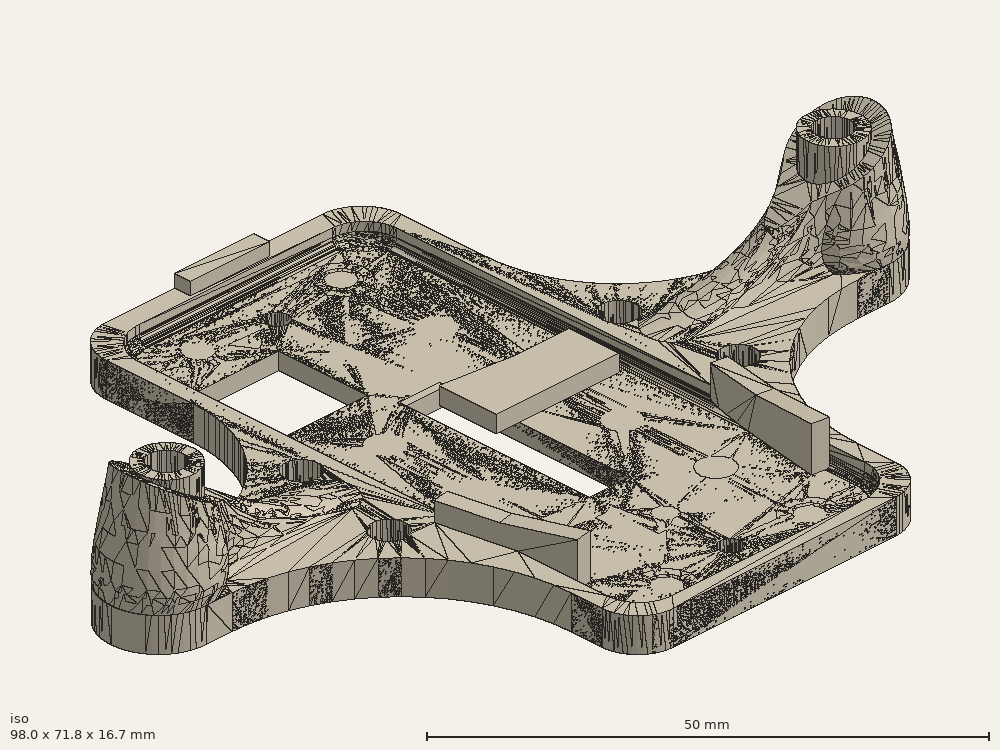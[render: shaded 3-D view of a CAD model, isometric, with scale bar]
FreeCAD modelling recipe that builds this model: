
FCSTD DOCUMENT  (FreeCAD 0.16R5446 (Git))
Label: iris_tarot_ng
License: CC-BY 3.0
LicenseURL: http://creativecommons.org/licenses/by/3.0/
objects: Part::Cylinder×19, Sketcher::SketchObject×15, Part::Cut×10, PartDesign::Pad×6, Part::Feature×4, Part::MultiFuse×4, Part::Loft×2, Part::Box×2, PartDesign::Fillet×2, PartDesign::Pocket×2, Mesh::Feature×1, PartDesign::LinearPattern×1, PartDesign::Chamfer×1
note: 76 computed .brp shape members not serialized (recipe doc carries the construction recipe); baked Part::Feature solids carry a one-line shape summary decoded from their .brp

FEATURE [Mesh::Feature] tarot_with_extra_spacing
FEATURE [Sketcher::SketchObject] Sketch
  Placement = pos=(4.5,0,4) rot=(0,0,1;0rad)
  sketch-geometry (4):
    g0: ArcOfCircle CenterX=-47.4503 CenterY=0 CenterZ=0 NormalX=0 NormalY=0 NormalZ=1 Radius=6 StartAngle=0.685014 EndAngle=5.53331
    g1: ArcOfCircle CenterX=-26.1247 CenterY=0 CenterZ=0 NormalX=0 NormalY=0 NormalZ=1 Radius=3 StartAngle=4.71239 EndAngle=7.61132
    g2: LineSegment StartX=-43.0597 StartY=-4.0893 StartZ=0 EndX=-26.1247 EndY=-3 EndZ=0
    g3: LineSegment StartX=-42.8038 StartY=3.7961 StartZ=0 EndX=-25.4039 EndY=2.91211 EndZ=0
  constraints (8):
    c: PointOnObject(g0,g-1)
    c: Radius(g0) = 6
    c: PointOnObject(g1,g-1)
    c: Radius(g1) = 3
    c: Coincident(g0,g3)
    c: Coincident(g1,g3)
    c: Coincident(g1,g2)
    c: Coincident(g0,g2)
FEATURE [Sketcher::SketchObject] Sketch001
  Placement = pos=(0,0,17) rot=(0,0,1;0rad)
  sketch-geometry (4):
    g0: ArcOfCircle CenterX=-42 CenterY=0 CenterZ=0 NormalX=0 NormalY=0 NormalZ=1 Radius=5 StartAngle=1.5708 EndAngle=4.71239
    g1: ArcOfCircle CenterX=-42 CenterY=0 CenterZ=0 NormalX=0 NormalY=0 NormalZ=1 Radius=4.93488 StartAngle=5.76091 EndAngle=6.78639
    g2: LineSegment StartX=-42 StartY=5 StartZ=0 EndX=-37.6768 EndY=2.37977 EndZ=0
    g3: LineSegment StartX=-42 StartY=-5 StartZ=0 EndX=-37.723 EndY=-2.46177 EndZ=0
  constraints (5):
    c: Radius(g0) = 5
    c: Coincident(g0,g2)
    c: Coincident(g1,g2)
    c: Coincident(g1,g3)
    c: Coincident(g0,g3)
FEATURE [Sketcher::SketchObject] Sketch002
  Placement = pos=(2.5,0,7.5) rot=(0,0,1;0rad)
  sketch-geometry (4):
    g0: ArcOfCircle CenterX=-45.3118 CenterY=0 CenterZ=0 NormalX=0 NormalY=0 NormalZ=1 Radius=6 StartAngle=0.523596 EndAngle=5.75959
    g1: ArcOfCircle CenterX=-35.9224 CenterY=0 CenterZ=0 NormalX=0 NormalY=0 NormalZ=1 Radius=2 StartAngle=4.93357 EndAngle=7.89275
    g2: LineSegment StartX=-40.1156 StartY=-2.99999 StartZ=0 EndX=-35.4836 EndY=-1.95128 EndZ=0
    g3: LineSegment StartX=-40.1156 StartY=2.99999 StartZ=0 EndX=-35.9999 EndY=1.9985 EndZ=0
  constraints (8):
    c: PointOnObject(g0,g-1)
    c: Radius(g0) = 6
    c: PointOnObject(g1,g-1)
    c: Radius(g1) = 2
    c: Coincident(g0,g3)
    c: Coincident(g1,g3)
    c: Coincident(g1,g2)
    c: Coincident(g0,g2)
FEATURE [Sketcher::SketchObject] Sketch003
  Placement = pos=(0,6,0) rot=(1,0,0;1.5708rad)
  sketch-geometry (4):
    g0: LineSegment StartX=-49.773 StartY=18.3055 StartZ=0 EndX=-31.5833 EndY=7.72916 EndZ=0
    g1: LineSegment StartX=-31.5833 StartY=7.72916 StartZ=0 EndX=-31.5833 EndY=19.3543 EndZ=0
    g2: LineSegment StartX=-31.5833 StartY=19.3543 StartZ=0 EndX=-49.773 EndY=19.3543 EndZ=0
    g3: LineSegment StartX=-49.773 StartY=19.3543 StartZ=0 EndX=-49.773 EndY=18.3055 EndZ=0
  constraints (7):
    c: Coincident(g0,g1)
    c: Vertical(g1)
    c: Coincident(g1,g2)
    c: Horizontal(g2)
    c: Coincident(g2,g3)
    c: Vertical(g3)
    c: Coincident(g0,g3)
FEATURE [PartDesign::Pad] Pad
  Length = 12
  Length2 = 100
  Placement = pos=(0,6,0) rot=(1,0,0;1.5708rad)
  Sketch = -> Sketch003
  Type = 0
FEATURE [Part::Loft] Loft
  Closed = false
  Ruled = false
  Sections = -> [Sketch,Sketch002,Sketch001]
  Solid = true
FEATURE [Part::Cylinder] Cylinder
  Angle = 360
  Height = 16
  Placement = pos=(-42,0,0) rot=(0,0,1;0rad)
  Radius = 3.35
FEATURE [Part::Feature] tarot_with_extra_spacing001
  shape: bbox 95 x 72 x 19 mm, 8458 faces, 0 solids (baked)
FEATURE [Part::Feature] tarot_with_extra_spacing002
  Placement = pos=(0,0,-30) rot=(0,0,1;0rad)
  shape: bbox 95 x 72 x 19 mm, 8458 faces, 0 solids (baked)
FEATURE [Sketcher::SketchObject] Sketch005
  sketch-geometry (30):
    g0: LineSegment StartX=-43.0008 StartY=-5.99913 StartZ=0 EndX=-39.7542 EndY=-5.99913 EndZ=0
    g1: LineSegment StartX=-18.4 StartY=-27.3533 StartZ=0 EndX=-18.4 EndY=-31.2517 EndZ=0
    g2: LineSegment StartX=-13.9033 StartY=-35.7484 StartZ=0 EndX=14.1218 EndY=-35.7484 EndZ=0
    g3: LineSegment StartX=18.4624 StartY=-31.4078 StartZ=0 EndX=18.4624 EndY=-26.4703 EndZ=0
    g4: LineSegment StartX=38.9278 StartY=-6.0049 StartZ=0 EndX=43 EndY=-6.0049 EndZ=0
    g5: LineSegment StartX=18.5876 StartY=20.3952 StartZ=0 EndX=18.5876 EndY=31.0167 EndZ=0
    g6: LineSegment StartX=13.6303 StartY=35.974 StartZ=0 EndX=-13.6463 EndY=35.974 EndZ=0
    g7: LineSegment StartX=-18.3887 StartY=31.2316 StartZ=0 EndX=-18.3887 EndY=20.2783 EndZ=0
    g8: ArcOfCircle CenterX=-34.8675 CenterY=20.2783 CenterZ=0 NormalX=0 NormalY=0 NormalZ=1 Radius=16.4788 StartAngle=4.76149 EndAngle=6.28319
    g9: ArcOfCircle CenterX=-13.6463 CenterY=31.2316 CenterZ=0 NormalX=0 NormalY=0 NormalZ=1 Radius=4.74244 StartAngle=1.5708 EndAngle=3.14159
    g10: ArcOfCircle CenterX=13.6303 CenterY=31.0167 CenterZ=0 NormalX=0 NormalY=0 NormalZ=1 Radius=4.95728 StartAngle=0 EndAngle=1.5708
    g11: ArcOfCircle CenterX=14.1218 CenterY=-31.4078 CenterZ=0 NormalX=0 NormalY=0 NormalZ=1 Radius=4.34063 StartAngle=4.71239 EndAngle=6.28319
    g12: ArcOfCircle CenterX=-13.9033 CenterY=-31.2517 CenterZ=0 NormalX=0 NormalY=0 NormalZ=1 Radius=4.49672 StartAngle=3.14159 EndAngle=4.71239
    g13: ArcOfCircle CenterX=-39.7542 CenterY=-27.3533 CenterZ=0 NormalX=0 NormalY=0 NormalZ=1 Radius=21.3542 StartAngle=0 EndAngle=1.5708
    g14: ArcOfCircle CenterX=38.9278 CenterY=-26.4703 CenterZ=0 NormalX=0 NormalY=0 NormalZ=1 Radius=20.4654 StartAngle=1.5708 EndAngle=3.14159
    g15: ArcOfCircle CenterX=35.1751 CenterY=20.3952 CenterZ=0 NormalX=0 NormalY=0 NormalZ=1 Radius=16.5875 StartAngle=3.14159 EndAngle=4.64696
    g16: LineSegment StartX=-14.9221 StartY=23.9362 StartZ=0 EndX=-3.92211 EndY=23.9362 EndZ=0
    g17: LineSegment StartX=-3.92211 StartY=23.9362 StartZ=0 EndX=-3.92211 EndY=12.7774 EndZ=0
    g18: LineSegment StartX=-3.92211 StartY=12.7774 StartZ=0 EndX=-14.9221 EndY=12.7774 EndZ=0
    g19: LineSegment StartX=-14.9221 StartY=12.7774 StartZ=0 EndX=-14.9221 EndY=23.9362 EndZ=0
    g20: LineSegment StartX=-2.79564 StartY=9.89253 StartZ=0 EndX=2.24186 EndY=9.89253 EndZ=0
    g21: LineSegment StartX=2.24186 StartY=9.89253 StartZ=0 EndX=2.24186 EndY=-14.0404 EndZ=0
    g22: LineSegment StartX=2.24186 StartY=-14.0404 StartZ=0 EndX=-2.79564 EndY=-14.0404 EndZ=0
    g23: LineSegment StartX=-2.79564 StartY=-14.0404 StartZ=0 EndX=-2.79564 EndY=9.89253 EndZ=0
    g24: ArcOfCircle CenterX=43.1085 CenterY=-13.8824 CenterZ=0 NormalX=0 NormalY=0 NormalZ=1 Radius=19.8876 StartAngle=1.57625 EndAngle=2.04142
    g25: ArcOfCircle CenterX=-43.1052 CenterY=-13.8609 CenterZ=0 NormalX=0 NormalY=0 NormalZ=1 Radius=19.8603 StartAngle=1.09785 EndAngle=1.56554
    g26: Circle CenterX=0 CenterY=28 CenterZ=0 NormalX=0 NormalY=0 NormalZ=1 Radius=1.25
    g27: Circle CenterX=0 CenterY=-29 CenterZ=0 NormalX=0 NormalY=0 NormalZ=1 Radius=1.25
    g28: ArcOfCircle CenterX=43 CenterY=0 CenterZ=0 NormalX=0 NormalY=0 NormalZ=1 Radius=6.0049 StartAngle=4.71239 EndAngle=7.85398
    g29: ArcOfCircle CenterX=-43 CenterY=0 CenterZ=0 NormalX=0 NormalY=0 NormalZ=1 Radius=5.99913 StartAngle=1.57092 EndAngle=4.71226
  constraints (50):
    c: Horizontal(g0)
    c: Vertical(g1)
    c: Horizontal(g2)
    c: Vertical(g3)
    c: Horizontal(g4)
    c: Vertical(g5)
    c: Horizontal(g6)
    c: Vertical(g7)
    c: Tangent(g7,g8) = 1.5708
    c: Tangent(g6,g9) = -1.5708
    c: Tangent(g7,g9) = -1.5708
    c: Tangent(g5,g10) = -1.5708
    c: Tangent(g6,g10) = -1.5708
    c: Tangent(g2,g11) = -1.5708
    c: Tangent(g3,g11) = -1.5708
    c: Tangent(g1,g12) = -1.5708
    c: Tangent(g2,g12) = -1.5708
    c: Tangent(g0,g13) = 1.5708
    c: Tangent(g1,g13) = 1.5708
    c: Tangent(g3,g14) = 1.5708
    c: Tangent(g4,g14) = 1.5708
    c: Tangent(g5,g15) = 1.5708
    c: Coincident(g16,g17)
    c: Coincident(g17,g18)
    c: Coincident(g18,g19)
    c: Coincident(g19,g16)
    c: Horizontal(g16)
    c: Horizontal(g18)
    c: Vertical(g17)
    c: Vertical(g19)
    c: Coincident(g20,g21)
    c: Coincident(g21,g22)
    c: Coincident(g22,g23)
    c: Coincident(g23,g20)
    c: Horizontal(g20)
    c: Horizontal(g22)
    c: Vertical(g21)
    c: Vertical(g23)
    c: Coincident(g15,g24)
    c: Coincident(g8,g25)
    c: PointOnObject(g26,g-2)
    c: PointOnObject(g27,g-2)
    c: Radius(g26) = 1.25
    c: Radius(g27) = 1.25
    c: PointOnObject(g28,g-1)
    c: Coincident(g4,g28)
    c: Coincident(g24,g28)
    c: PointOnObject(g29,g-1)
    c: Coincident(g0,g29)
    c: Coincident(g25,g29)
FEATURE [Sketcher::SketchObject] Sketch006
  Placement = pos=(0,0,2) rot=(0,0,1;0rad)
  sketch-geometry (8):
    g0: LineSegment StartX=-11.8034 StartY=33.6358 StartZ=0 EndX=12.4871 EndY=33.6358 EndZ=0
    g1: LineSegment StartX=16.5418 StartY=29.5811 StartZ=0 EndX=16.5418 EndY=-29.2964 EndZ=0
    g2: LineSegment StartX=11.7818 StartY=-34.0564 StartZ=0 EndX=-12.4109 EndY=-34.0564 EndZ=0
    g3: LineSegment StartX=-16.5144 StartY=-29.9528 StartZ=0 EndX=-16.5144 EndY=28.9247 EndZ=0
    g4: ArcOfCircle CenterX=-11.8034 CenterY=28.9247 CenterZ=0 NormalX=0 NormalY=0 NormalZ=1 Radius=4.71109 StartAngle=1.5708 EndAngle=3.14159
    g5: ArcOfCircle CenterX=12.4871 CenterY=29.5811 CenterZ=0 NormalX=0 NormalY=0 NormalZ=1 Radius=4.05471 StartAngle=0 EndAngle=1.5708
    g6: ArcOfCircle CenterX=11.7818 CenterY=-29.2964 CenterZ=0 NormalX=0 NormalY=0 NormalZ=1 Radius=4.75994 StartAngle=4.71239 EndAngle=6.28319
    g7: ArcOfCircle CenterX=-12.4109 CenterY=-29.9528 CenterZ=0 NormalX=0 NormalY=0 NormalZ=1 Radius=4.10356 StartAngle=3.14159 EndAngle=4.71239
  constraints (12):
    c: Horizontal(g0)
    c: Horizontal(g2)
    c: Vertical(g1)
    c: Vertical(g3)
    c: Tangent(g0,g4) = 1.5708
    c: Tangent(g3,g4) = 1.5708
    c: Tangent(g0,g5) = 1.5708
    c: Tangent(g1,g5) = 1.5708
    c: Tangent(g1,g6) = 1.5708
    c: Tangent(g2,g6) = 1.5708
    c: Tangent(g2,g7) = 1.5708
    c: Tangent(g3,g7) = 1.5708
FEATURE [PartDesign::Pad] Pad002
  Length = 4
  Length2 = 100
  Sketch = -> Sketch005
  Type = 0
FEATURE [PartDesign::Pad] Pad003
  Length = 2
  Length2 = 100
  Placement = pos=(0,0,2) rot=(0,0,1;0rad)
  Sketch = -> Sketch006
  Type = 0
FEATURE [Part::Cut] Cut003006
  Base = -> Pad002
  Tool = -> Pad003
FEATURE [Part::Box] Box  label="Cube"
  Height = 5.5
  Length = 10
  Placement = pos=(-5,34,0) rot=(0,0,1;0rad)
  Width = 2
FEATURE [Sketcher::SketchObject] Sketch007
  Placement = pos=(15,0,10) rot=(0,0,1;0rad)
  sketch-geometry (5):
    g0: LineSegment StartX=-25.413 StartY=-2.7359 StartZ=0 EndX=-25.413 EndY=-10 EndZ=0
    g1: LineSegment StartX=-25.413 StartY=-10 StartZ=0 EndX=-10 EndY=-10 EndZ=0
    g2: LineSegment StartX=-10 StartY=-10 StartZ=0 EndX=-10 EndY=-3.71578 EndZ=0
    g3: LineSegment StartX=-10 StartY=-3.71578 StartZ=0 EndX=-17 EndY=-3.71578 EndZ=0
    g4: LineSegment StartX=-17 StartY=-3.71578 StartZ=0 EndX=-25.413 EndY=-2.7359 EndZ=0
  constraints (9):
    c: Vertical(g0)
    c: Coincident(g0,g1)
    c: Horizontal(g1)
    c: Coincident(g1,g2)
    c: Vertical(g2)
    c: Coincident(g2,g3)
    c: Horizontal(g3)
    c: Coincident(g3,g4)
    c: Coincident(g4,g0)
FEATURE [PartDesign::Pad] Pad004
  Length = 2
  Length2 = 100
  Placement = pos=(15,0,10) rot=(0,0,1;0rad)
  Sketch = -> Sketch007
  Type = 0
FEATURE [Part::Feature] Pad006
  Placement = pos=(-20,-0.0923,10) rot=(0.506366,0.609751,0.609751;2.20414rad)
  shape: bbox 4.797 x 15.52 x 7.264 mm, 7 faces (baked)
FEATURE [Part::Feature] Pad007
  Placement = pos=(18.0704,-0.0923,10) rot=(0.639118,0.543842,0.543842;2.00421rad)
  shape: bbox 4.441 x 15.53 x 7.264 mm, 7 faces (baked)
FEATURE [Part::Cylinder] Cylinder008
  Angle = 360
  Height = 2
  Placement = pos=(-42,0,0) rot=(0,0,1;0rad)
  Radius = 4
FEATURE [Part::Cylinder] Cylinder009
  Angle = 360
  Height = 2
  Placement = pos=(42,0,0) rot=(0,0,1;0rad)
  Radius = 4
FEATURE [Part::Cylinder] Cylinder010
  Angle = 360
  Height = 10
  Placement = pos=(-22,-8,0) rot=(0,0,1;0rad)
  Radius = 2
FEATURE [Part::Cylinder] Cylinder013
  Angle = 360
  Height = 10
  Placement = pos=(22,-8,0) rot=(0,0,1;0rad)
  Radius = 2
FEATURE [Sketcher::SketchObject] Sketch009
  Placement = pos=(0,0,2) rot=(0,0,1;0rad)
  sketch-geometry (1):
    g0: Circle CenterX=9 CenterY=29 CenterZ=0 NormalX=0 NormalY=0 NormalZ=1 Radius=2.01767
FEATURE [Sketcher::SketchObject] Sketch011
  Placement = pos=(0,-2,0) rot=(0,0,1;0rad)
  sketch-geometry (2):
    g0: Circle CenterX=-20 CenterY=7 CenterZ=0 NormalX=0 NormalY=0 NormalZ=1 Radius=2.00106
    g1: Circle CenterX=20 CenterY=7 CenterZ=0 NormalX=0 NormalY=0 NormalZ=1 Radius=2.04465
  constraints (1):
    c: Symmetric(g1,g0,g-2)
FEATURE [PartDesign::Pad] Pad008
  Length = 10
  Length2 = 100
  Placement = pos=(0,-2,0) rot=(0,0,1;0rad)
  Sketch = -> Sketch011
  Type = 0
FEATURE [Part::Cylinder] Cylinder014
  Angle = 360
  Height = 19
  Placement = pos=(-42,0,0) rot=(0,0,1;0rad)
  Radius = 2
FEATURE [Part::Cylinder] Cylinder015
  Angle = 360
  Height = 19
  Placement = pos=(42,0,0) rot=(0,0,1;0rad)
  Radius = 2
FEATURE [Part::Cut] Cut
  Base = -> Loft
  Tool = -> Pad
FEATURE [Sketcher::SketchObject] Sketch014
  Placement = pos=(4.5,0,4) rot=(0,0,1;0rad)
  sketch-geometry (4):
    g0: ArcOfCircle CenterX=-47.4503 CenterY=0 CenterZ=0 NormalX=0 NormalY=0 NormalZ=1 Radius=6 StartAngle=0.685014 EndAngle=5.53331
    g1: ArcOfCircle CenterX=-26.1247 CenterY=0 CenterZ=0 NormalX=0 NormalY=0 NormalZ=1 Radius=3 StartAngle=4.71239 EndAngle=7.61132
    g2: LineSegment StartX=-43.0597 StartY=-4.0893 StartZ=0 EndX=-26.1247 EndY=-3 EndZ=0
    g3: LineSegment StartX=-42.8038 StartY=3.7961 StartZ=0 EndX=-25.4039 EndY=2.91211 EndZ=0
  constraints (8):
    c: PointOnObject(g0,g-1)
    c: Radius(g0) = 6
    c: PointOnObject(g1,g-1)
    c: Radius(g1) = 3
    c: Coincident(g0,g3)
    c: Coincident(g1,g3)
    c: Coincident(g1,g2)
    c: Coincident(g0,g2)
FEATURE [Sketcher::SketchObject] Sketch015
  Placement = pos=(0,0,17) rot=(0,0,1;0rad)
  sketch-geometry (4):
    g0: ArcOfCircle CenterX=-42 CenterY=0 CenterZ=0 NormalX=0 NormalY=0 NormalZ=1 Radius=5 StartAngle=1.5708 EndAngle=4.71239
    g1: ArcOfCircle CenterX=-42 CenterY=0 CenterZ=0 NormalX=0 NormalY=0 NormalZ=1 Radius=4.93488 StartAngle=5.76091 EndAngle=6.78639
    g2: LineSegment StartX=-42 StartY=5 StartZ=0 EndX=-37.6768 EndY=2.37977 EndZ=0
    g3: LineSegment StartX=-42 StartY=-5 StartZ=0 EndX=-37.723 EndY=-2.46177 EndZ=0
  constraints (5):
    c: Radius(g0) = 5
    c: Coincident(g0,g2)
    c: Coincident(g1,g2)
    c: Coincident(g1,g3)
    c: Coincident(g0,g3)
FEATURE [Sketcher::SketchObject] Sketch016
  Placement = pos=(2.5,0,7.5) rot=(0,0,1;0rad)
  sketch-geometry (4):
    g0: ArcOfCircle CenterX=-45.3118 CenterY=0 CenterZ=0 NormalX=0 NormalY=0 NormalZ=1 Radius=6 StartAngle=0.523596 EndAngle=5.75959
    g1: ArcOfCircle CenterX=-35.9224 CenterY=0 CenterZ=0 NormalX=0 NormalY=0 NormalZ=1 Radius=2 StartAngle=4.93357 EndAngle=7.89275
    g2: LineSegment StartX=-40.1156 StartY=-2.99999 StartZ=0 EndX=-35.4836 EndY=-1.95128 EndZ=0
    g3: LineSegment StartX=-40.1156 StartY=2.99999 StartZ=0 EndX=-35.9999 EndY=1.9985 EndZ=0
  constraints (8):
    c: PointOnObject(g0,g-1)
    c: Radius(g0) = 6
    c: PointOnObject(g1,g-1)
    c: Radius(g1) = 2
    c: Coincident(g0,g3)
    c: Coincident(g1,g3)
    c: Coincident(g1,g2)
    c: Coincident(g0,g2)
FEATURE [Sketcher::SketchObject] Sketch017
  Placement = pos=(0,6,0) rot=(1,0,0;1.5708rad)
  sketch-geometry (4):
    g0: LineSegment StartX=-49.773 StartY=18.3055 StartZ=0 EndX=-31.5833 EndY=7.72916 EndZ=0
    g1: LineSegment StartX=-31.5833 StartY=7.72916 StartZ=0 EndX=-31.5833 EndY=19.3543 EndZ=0
    g2: LineSegment StartX=-31.5833 StartY=19.3543 StartZ=0 EndX=-49.773 EndY=19.3543 EndZ=0
    g3: LineSegment StartX=-49.773 StartY=19.3543 StartZ=0 EndX=-49.773 EndY=18.3055 EndZ=0
  constraints (7):
    c: Coincident(g0,g1)
    c: Vertical(g1)
    c: Coincident(g1,g2)
    c: Horizontal(g2)
    c: Coincident(g2,g3)
    c: Vertical(g3)
    c: Coincident(g0,g3)
FEATURE [PartDesign::Pad] Pad009
  Length = 12
  Length2 = 100
  Placement = pos=(0,6,0) rot=(1,0,0;1.5708rad)
  Sketch = -> Sketch017
  Type = 0
FEATURE [Part::Loft] Loft001
  Closed = false
  Ruled = false
  Sections = -> [Sketch014,Sketch016,Sketch015]
  Solid = true
FEATURE [Part::Cylinder] Cylinder016
  Angle = 360
  Height = 16
  Placement = pos=(42,0,0) rot=(0,0,1;0rad)
  Radius = 3.35
FEATURE [Part::Cut] Cut003007
  Base = -> Loft001
  Placement = pos=(0,0,0) rot=(0,0,1;3.14159rad)
  Tool = -> Pad009
FEATURE [PartDesign::Fillet] Fillet
  Base = -> Cut003006 [Edge100,Edge103,Edge114,Edge112,Edge111,Edge108,Edge104,Edge107]
  Radius = 1
FEATURE [Part::MultiFuse] Fusion
  Shapes = -> [Pad006,Box,Pad007,Cylinder,Cut,Cylinder016,Cut003007,Fillet]
FEATURE [Part::MultiFuse] Fusion001
  Shapes = -> [Pad008,Cylinder014,Cylinder009,Cylinder010,Cylinder013,Cylinder008,Cylinder015]
FEATURE [Part::Cut] Cut003008
  Base = -> Fusion
  Tool = -> Fusion001
FEATURE [Sketcher::SketchObject] Sketch013
  Placement = pos=(0,0,2) rot=(0,0,1;0rad)
  Support = -> Cut003008 [Face91]
  sketch-geometry (2):
    g0: Circle CenterX=-9 CenterY=29 CenterZ=0 NormalX=0 NormalY=0 NormalZ=1 Radius=2
    g1: Circle CenterX=9 CenterY=29 CenterZ=0 NormalX=0 NormalY=0 NormalZ=1 Radius=2
FEATURE [PartDesign::Pocket] Pocket
  Length = 5
  Sketch = -> Sketch013
  Type = 0
FEATURE [PartDesign::LinearPattern] LinearPattern
  Direction = -> Sketch013 [V_Axis]
  Length = 59
  Occurrences = 6
  Originals = -> [Pocket]
  Reversed = true
FEATURE [Sketcher::SketchObject] Sketch012
  Placement = pos=(0,0,2) rot=(0,0,1;0rad)
  Support = -> LinearPattern [Face101]
  sketch-geometry (7):
    g0: LineSegment StartX=-5 StartY=-17 StartZ=0 EndX=-3 EndY=-17 EndZ=0
    g1: LineSegment StartX=-3 StartY=-17 StartZ=0 EndX=-3 EndY=-23 EndZ=0
    g2: LineSegment StartX=-3 StartY=-23 StartZ=0 EndX=-2 EndY=-23 EndZ=0
    g3: LineSegment StartX=-2 StartY=-23 StartZ=0 EndX=-4 EndY=-25 EndZ=0
    g4: LineSegment StartX=-4 StartY=-25 StartZ=0 EndX=-6 EndY=-23 EndZ=0
    g5: LineSegment StartX=-6 StartY=-23 StartZ=0 EndX=-5 EndY=-23 EndZ=0
    g6: LineSegment StartX=-5 StartY=-23 StartZ=0 EndX=-5 EndY=-17 EndZ=0
  constraints (12):
    c: Horizontal(g0)
    c: Coincident(g0,g1)
    c: Vertical(g1)
    c: Coincident(g1,g2)
    c: Horizontal(g2)
    c: Coincident(g2,g3)
    c: Coincident(g3,g4)
    c: Coincident(g4,g5)
    c: Horizontal(g5)
    c: Coincident(g5,g6)
    c: Coincident(g6,g0)
    c: Vertical(g6)
FEATURE [PartDesign::Pocket] Pocket001
  Length = 1
  Sketch = -> Sketch012
  Type = 0
FEATURE [PartDesign::Fillet] Fillet001
  Base = -> Pocket001 [Edge159,Edge121]
  Radius = 10
FEATURE [PartDesign::Chamfer] Chamfer
  Base = -> Fillet001 [Edge296,Edge285]
  Size = 1.9
FEATURE [Part::Cylinder] Cylinder017
  Angle = 360
  Height = 2
  Radius = 3
FEATURE [Part::Cylinder] Cylinder018
  Angle = 360
  Height = 2
  Radius = 1.5
FEATURE [Part::Cut] Cut003009
  Base = -> Cylinder017
  Placement = pos=(-9,29,0) rot=(0,0,1;0rad)
  Tool = -> Cylinder018
FEATURE [Part::Cylinder] Cylinder019
  Angle = 360
  Height = 2
  Radius = 3
FEATURE [Part::Cylinder] Cylinder020
  Angle = 360
  Height = 2
  Radius = 1.5
FEATURE [Part::Cut] Cut003010
  Base = -> Cylinder019
  Placement = pos=(9,29,0) rot=(0,0,1;0rad)
  Tool = -> Cylinder020
FEATURE [Part::Cylinder] Cylinder021
  Angle = 360
  Height = 2
  Radius = 3
FEATURE [Part::Cylinder] Cylinder022
  Angle = 360
  Height = 2
  Radius = 1.5
FEATURE [Part::Cut] Cut003011
  Base = -> Cylinder021
  Placement = pos=(9,-30,0) rot=(0,0,1;0rad)
  Tool = -> Cylinder022
FEATURE [Part::Cylinder] Cylinder023
  Angle = 360
  Height = 2
  Radius = 3
FEATURE [Part::Cylinder] Cylinder024
  Angle = 360
  Height = 2
  Radius = 1.5
FEATURE [Part::Cut] Cut003012
  Base = -> Cylinder023
  Placement = pos=(-9,-30,0) rot=(0,0,1;0rad)
  Tool = -> Cylinder024
FEATURE [Part::Cylinder] Cylinder025
  Angle = 360
  Height = 2
  Placement = pos=(9,17,0) rot=(0,0,1;0rad)
  Radius = 2
FEATURE [Part::Cut] Cut003013
  Base = -> Chamfer
  Tool = -> Cylinder025
FEATURE [Part::Box] Box001  label="Cube001"
  Height = 2
  Length = 5.4
  Placement = pos=(-3,9,0) rot=(0,0,1;0rad)
  Width = 1
FEATURE [Part::Cylinder] Cylinder026
  Angle = 360
  Height = 10
  Placement = pos=(0,19.75,0) rot=(0,0,1;0rad)
  Radius = 1.25
FEATURE [Part::Cylinder] Cylinder027
  Angle = 360
  Height = 10
  Placement = pos=(0,-20.75,0) rot=(0,0,1;0rad)
  Radius = 1.25
FEATURE [Part::MultiFuse] Fusion004
  Shapes = -> [Cylinder026,Cylinder027]
FEATURE [Part::MultiFuse] Fusion005
  Shapes = -> [Box001,Cut003009,Cut003010,Cut003011,Cut003012,Cut003013]
FEATURE [Part::Cut] Cut003014
  Base = -> Fusion005
  Tool = -> Fusion004
